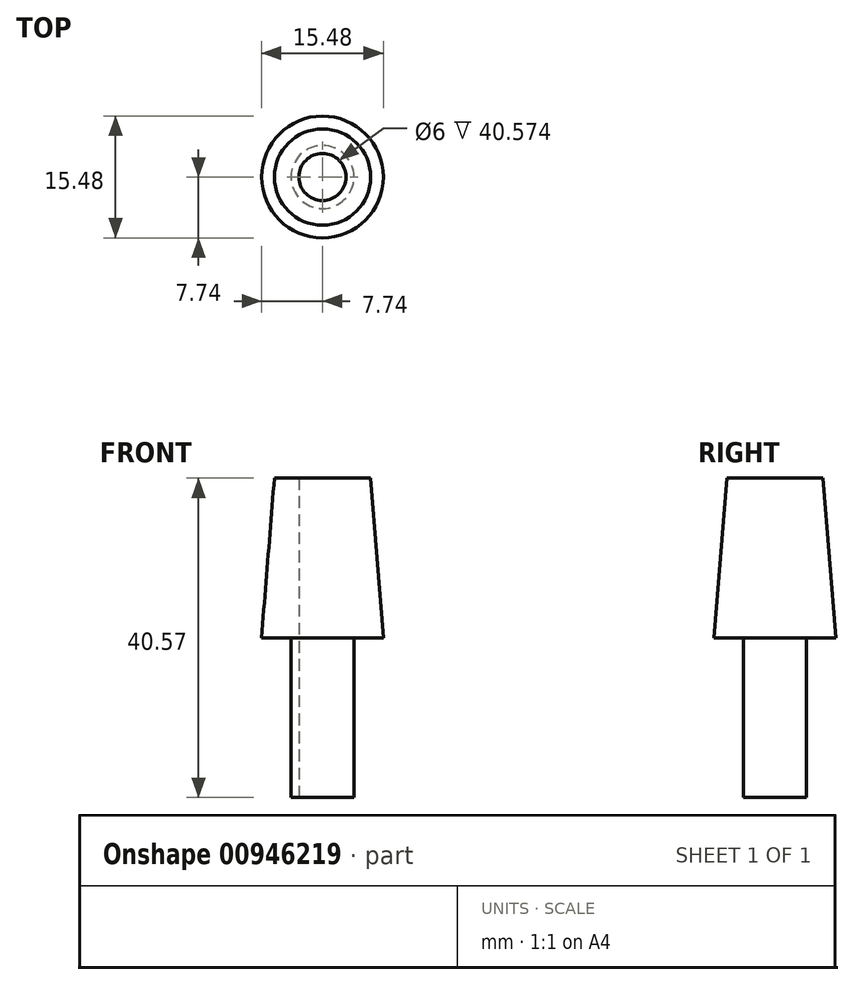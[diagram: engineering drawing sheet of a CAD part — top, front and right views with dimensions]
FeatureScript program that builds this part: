
annotation { "Feature Type Name" : "Feature", "Feature Type Description" : "" }
export const myFeature = defineFeature(function(context is Context, id is Id, definition is map)
    precondition{}
    {
        {
            var Q0;
            Q0=qCreatedBy(makeId("Front.planeOp"),FACE);
            var sketch = newSketch(context, id + "F0", { "sketchPlane" : qUnion([Q0])});
            skLineSegment(sketch, "E0", {"start": v(0, 0) * mm, "end": v(0, 40.57) * mm});
            skLineSegment(sketch, "E1", {"start": v(0, 40.57) * mm, "end": v(6.11, 40.57) * mm});
            skLineSegment(sketch, "E2", {"start": v(6.11, 40.57) * mm, "end": v(7.74, 20.29) * mm});
            skLineSegment(sketch, "E3", {"start": v(0, 0) * mm, "end": v(4, 0) * mm});
            skLineSegment(sketch, "E4", {"start": v(4, 0) * mm, "end": v(4, 20.29) * mm});
            skLineSegment(sketch, "E5", {"start": v(4, 20.28) * mm, "end": v(7.74, 20.29) * mm});
            skSolve(sketch);
        }
        {
            var Q0;
            Q0=makeQuery(id+"F0.imprint","IMPRINT",FACE,{"disambiguationData":[TD([[makeQuery(id+"F0.imprint","IMPRINT",EDGE,{"derivedFrom":sQuery(id+"F0.wireOp",EDGE,"E0")}),-1.0]])]});
            var Q1;
            Q1=sQuery(id+"F0.wireOp",EDGE,"E0");
            revolve(context, id + "F1", {"surfaceOperationType" : NewSurfaceOperationType.NEW, "entities" : qUnion([Q0]), "axis" : qUnion([Q1]), "revolveType" : RevolveType.FULL});
        }
        {
            var Q0;
            Q0=qCreatedBy(makeId("Top.planeOp"),FACE);
            var sketch = newSketch(context, id + "F2", { "sketchPlane" : qUnion([Q0])});
            skCircle(sketch, "E6", {"center": v(0, 0) * mm, "radius": 3 * mm});
            skSolve(sketch);
        }
        {
            var Q0;
            Q0 = qSketchRegion(id + "F2", true);
            var Q1;
            Q1=makeQuery(id+"F1.opRevolve","SWEPT_FACE",FACE,{"disambiguationData":[OSD([sQuery(id+"F0.wireOp",EDGE,"E1")])]});
            extrude(context, id + "F3", {"entities" : qUnion([Q0, Q1]), "operationType" : NewBodyOperationType.REMOVE, "depth" : 61 * mm, "offsetDistance" : 25 * mm});
        }
    });
